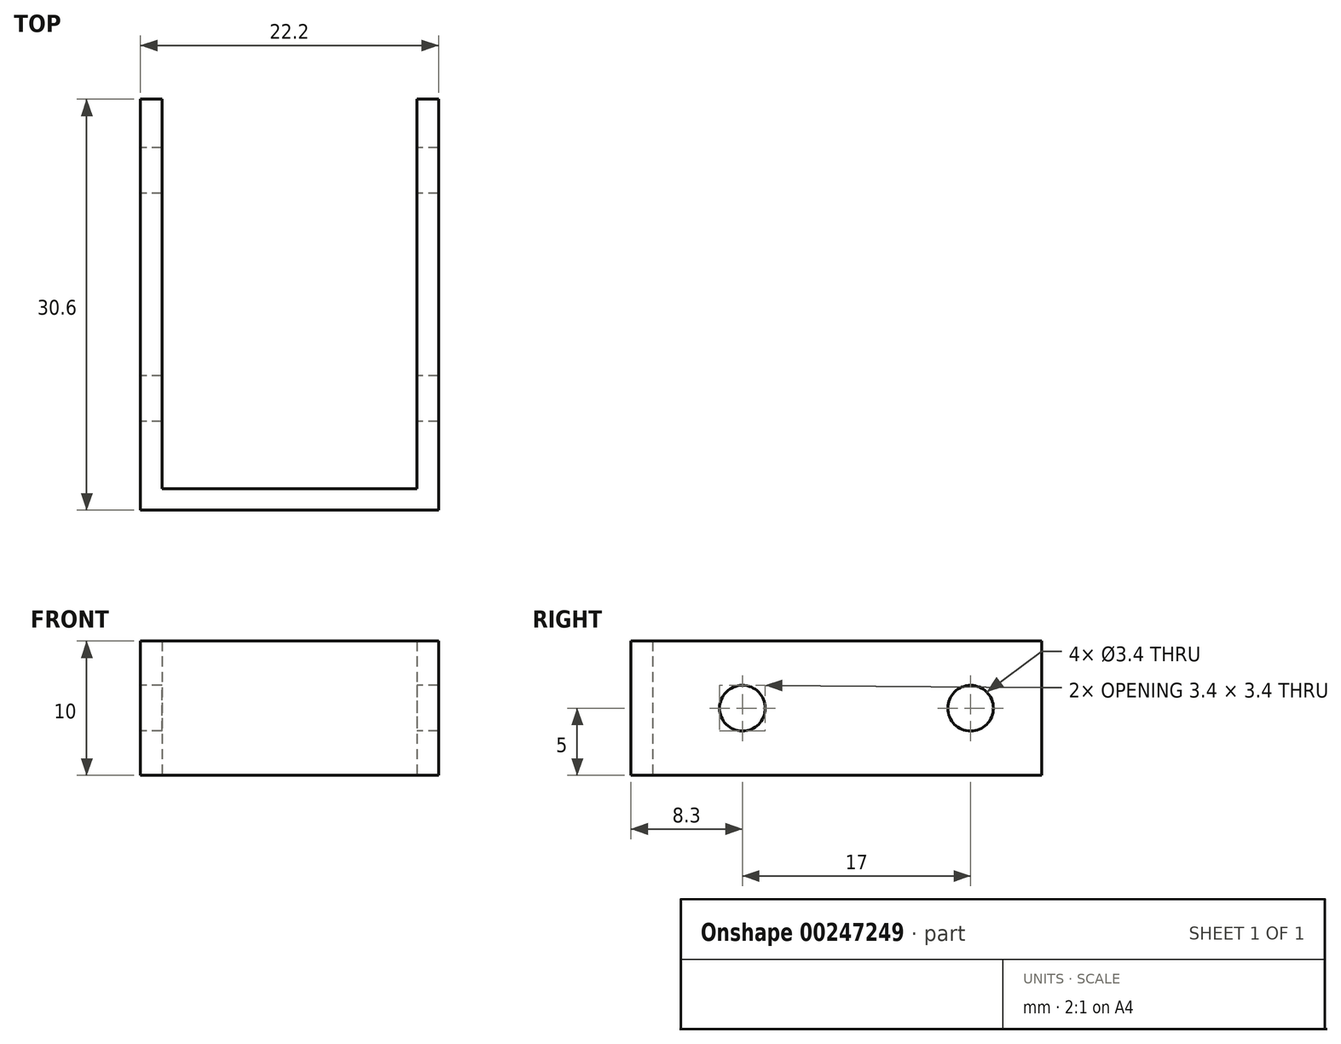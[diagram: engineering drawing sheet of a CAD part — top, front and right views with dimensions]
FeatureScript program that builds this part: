
annotation { "Feature Type Name" : "Feature", "Feature Type Description" : "" }
export const myFeature = defineFeature(function(context is Context, id is Id, definition is map)
    precondition{}
    {
        {
            var Q0;
            Q0=qCreatedBy(makeId("Top.planeOp"),FACE);
            var sketch = newSketch(context, id + "F0", { "sketchPlane" : qUnion([Q0])});
            skLineSegment(sketch, "E0", {"start": v(0, 0) * mm, "end": v(0, 1.6) * mm});
            skLineSegment(sketch, "E1", {"start": v(0, 1.6) * mm, "end": v(0, 5.6) * mm});
            skLineSegment(sketch, "E2", {"start": v(0, 5.6) * mm, "end": v(0, 30.6) * mm});
            skLineSegment(sketch, "E3", {"start": v(0, 30.6) * mm, "end": v(1.6, 30.6) * mm});
            skLineSegment(sketch, "E4", {"start": v(1.6, 30.6) * mm, "end": v(1.6, 5.6) * mm});
            skLineSegment(sketch, "E5", {"start": v(1.6, 5.6) * mm, "end": v(1.6, 1.6) * mm});
            skLineSegment(sketch, "E6", {"start": v(1.6, 1.6) * mm, "end": v(20.6, 1.6) * mm});
            skLineSegment(sketch, "E7", {"start": v(20.6, 1.6) * mm, "end": v(20.6, 5.6) * mm});
            skLineSegment(sketch, "E8", {"start": v(20.6, 5.6) * mm, "end": v(20.6, 30.6) * mm});
            skLineSegment(sketch, "E9", {"start": v(20.6, 30.6) * mm, "end": v(22.2, 30.6) * mm});
            skLineSegment(sketch, "E10", {"start": v(22.2, 30.6) * mm, "end": v(22.2, 5.6) * mm});
            skLineSegment(sketch, "E11", {"start": v(22.2, 5.6) * mm, "end": v(22.2, 1.6) * mm});
            skLineSegment(sketch, "E12", {"start": v(22.2, 1.6) * mm, "end": v(22.2, 0) * mm});
            skLineSegment(sketch, "E13", {"start": v(22.2, 0) * mm, "end": v(0, 0) * mm});
            skSolve(sketch);
        }
        {
            var Q0;
            Q0 = qSketchRegion(id + "F0", true);
            extrude(context, id + "F1", {"entities" : qUnion([Q0]), "depth" : 10 * mm});
        }
        {
            var Q0;
            Q0=makeQuery(id+"F1.opExtrude","SWEPT_FACE",FACE,{"disambiguationData":[OSD([sQuery(id+"F0.wireOp",EDGE,"E0"),sQuery(id+"F0.wireOp",EDGE,"E1"),sQuery(id+"F0.wireOp",EDGE,"E2")])]});
            var sketch = newSketch(context, id + "F2", { "sketchPlane" : qUnion([Q0])});
            skLineSegment(sketch, "E14", {"start": v(-30.6, 5) * mm, "end": v(-27, 5) * mm, "construction": true});
            skLineSegment(sketch, "E15", {"start": v(0, 5) * mm, "end": v(-6.6, 5) * mm, "construction": true});
            skLineSegment(sketch, "E16", {"start": v(-27, 5) * mm, "end": v(-25.3, 5) * mm, "construction": true});
            skCircle(sketch, "E17", {"center": v(-25.3, 5) * mm, "radius": 1.7 * mm});
            skLineSegment(sketch, "E18", {"start": v(-6.6, 5) * mm, "end": v(-8.3, 5) * mm, "construction": true});
            skCircle(sketch, "E19", {"center": v(-8.3, 5) * mm, "radius": 1.7 * mm});
            skSolve(sketch);
        }
        {
            var Q0;
            Q0=makeQuery(id+"F2.imprint","IMPRINT",FACE,{"disambiguationData":[TD([[makeQuery(id+"F2.imprint","IMPRINT",EDGE,{"derivedFrom":sQuery(id+"F2.wireOp",EDGE,"E17")}),1.0]])]});
            var Q1;
            Q1=makeQuery(id+"F2.imprint","IMPRINT",FACE,{"disambiguationData":[TD([[makeQuery(id+"F2.imprint","IMPRINT",EDGE,{"derivedFrom":sQuery(id+"F2.wireOp",EDGE,"E19")}),1.0]])]});
            extrude(context, id + "F3", {"entities" : qUnion([Q0, Q1]), "operationType" : NewBodyOperationType.REMOVE, "endBound" : BoundingType.THROUGH_ALL, "oppositeDirection" : true, "depth" : 25 * mm});
        }
    });
